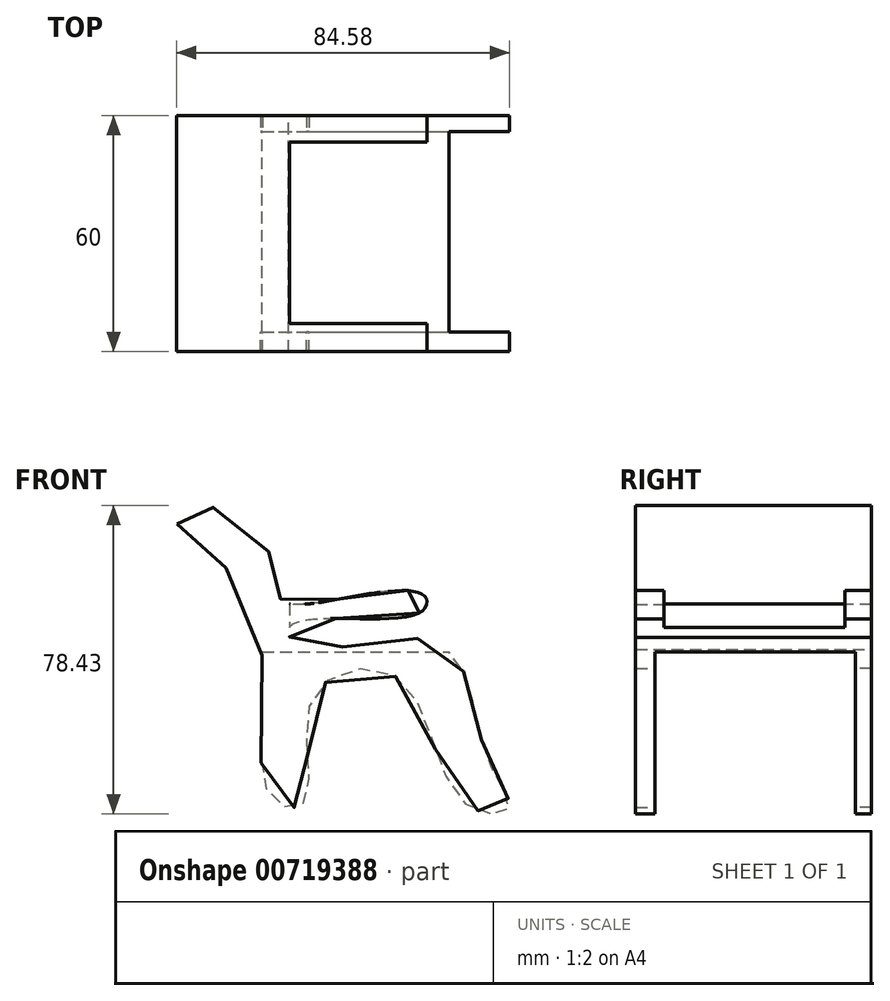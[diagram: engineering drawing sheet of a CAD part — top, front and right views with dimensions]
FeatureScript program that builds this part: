
annotation { "Feature Type Name" : "Feature", "Feature Type Description" : "" }
export const myFeature = defineFeature(function(context is Context, id is Id, definition is map)
    precondition{}
    {
        {
            var Q0;
            Q0=qCreatedBy(makeId("Front.planeOp"),FACE);
            var sketch = newSketch(context, id + "F0", { "sketchPlane" : qUnion([Q0])});
            skFitSpline(sketch, "E0", {"points": [v(-48.98, 39.24) * mm, v(-30.08, 19.57) * mm, v(-25.68, -29.31) * mm, v(-16.52, -31.22) * mm, v(-14.42, -4.87) * mm, v(7.35, 0) * mm, v(23.4, -31.03) * mm, v(35.23, -33.13) * mm, v(30.08, -20.72) * mm, v(23.01, 3.34) * mm, v(7.35, 10.4) * mm, v(-17.85, 8.12) * mm, v(-19.76, 13.65) * mm, v(11.93, 16.33) * mm, v(14.04, 20.9) * mm, v(-3.91, 20.9) * mm, v(-22.44, 19.95) * mm, v(-25.11, 31.03) * mm, v(-43.44, 44.02) * mm, v(-48.98, 39.24) * mm]});
            skSolve(sketch);
        }
        {
            var Q0;
            Q0 = qSketchRegion(id + "F0", true);
            extrude(context, id + "F1", {"entities" : qUnion([Q0]), "depth" : 60 * mm, "offsetDistance" : 25.4 * mm});
        }
        {
            var Q0;
            Q0=qCreatedBy(makeId("Right.planeOp"),FACE);
            var sketch = newSketch(context, id + "F2", { "sketchPlane" : qUnion([Q0])});
            skLineSegment(sketch, "E1.bottom", {"start": v(-55.05, 6.72) * mm, "end": v(-4.06, 6.72) * mm});
            skLineSegment(sketch, "E1.top", {"start": v(-55.05, -38.34) * mm, "end": v(-4.06, -38.34) * mm});
            skLineSegment(sketch, "E1.left", {"start": v(-55.05, 6.72) * mm, "end": v(-55.05, -38.34) * mm});
            skLineSegment(sketch, "E1.right", {"start": v(-4.06, 6.72) * mm, "end": v(-4.06, -38.34) * mm});
            skSolve(sketch);
        }
        {
            var Q0;
            Q0 = qSketchRegion(id + "F2", true);
            extrude(context, id + "F3", {"entities" : qUnion([Q0]), "operationType" : NewBodyOperationType.REMOVE, "oppositeDirection" : true, "depth" : 51.5 * mm, "offsetDistance" : 25 * mm, "hasSecondDirection" : true, "secondDirectionOppositeDirection" : false, "secondDirectionDepth" : 59.7 * mm});
        }
        {
            var Q0;
            Q0=qCreatedBy(makeId("Top.planeOp"),FACE);
            var sketch = newSketch(context, id + "F4", { "sketchPlane" : qUnion([Q0])});
            skLineSegment(sketch, "E2.bottom", {"start": v(-20.34, -6.78) * mm, "end": v(16.52, -6.78) * mm});
            skLineSegment(sketch, "E2.top", {"start": v(-20.34, -52.8) * mm, "end": v(16.52, -52.8) * mm});
            skLineSegment(sketch, "E2.left", {"start": v(-20.34, -6.78) * mm, "end": v(-20.34, -52.8) * mm});
            skLineSegment(sketch, "E2.right", {"start": v(16.52, -6.78) * mm, "end": v(16.52, -52.8) * mm});
            skSolve(sketch);
        }
        {
            var Q0;
            Q0 = qSketchRegion(id + "F4", true);
            extrude(context, id + "F5", {"entities" : qUnion([Q0]), "operationType" : NewBodyOperationType.REMOVE, "depth" : 34.3 * mm, "offsetDistance" : 25 * mm, "hasSecondDirection" : true, "secondDirectionOppositeDirection" : false, "secondDirectionDepth" : 11.6 * mm});
        }
    });
